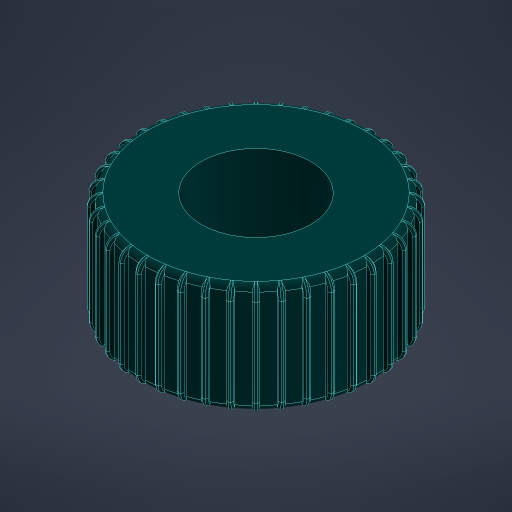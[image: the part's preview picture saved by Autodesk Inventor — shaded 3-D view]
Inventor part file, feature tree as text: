
AUTODESK INVENTOR PART (.ipt)
format: ipt  version: 2024 (Build 280153000, 153)  size: 1,063,424 bytes
history: native  units: mm
features: extrude x2, fillet x2, sketch x2, other x1, chamfer x1, pattern_circular x1
ambient origin geometry x8: Origin, YZ Plane, XZ Plane, XY Plane, X Axis, Y Axis, Z Axis, Center Point
bodies: Body1 (feature_tree)
feature tree (9):
  other  "Твердое тело1"
  extrude  "Выдавливание1"  Depth=60.0mm
  extrude  "Выдавливание2"  Depth=125.0mm
  fillet  "Сопряжение2"  Radius=60.0mm
  chamfer  "Фаска1"  Distance=3.0mm
  pattern_circular  "Круговой массив1"  [2 undecoded]
  fillet  "Сопряжение3"  [1 undecoded]
  sketch  "Эскиз1"
  sketch  "Эскиз3"
note: 3 required parameter values undecoded (feature->parameter linkage not recoverable at this tier; creation-order binding heuristic only, values carry confidence <= 0.55)
